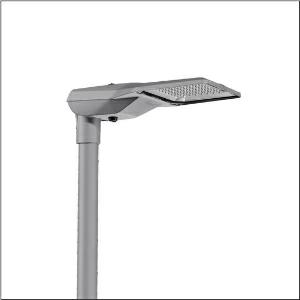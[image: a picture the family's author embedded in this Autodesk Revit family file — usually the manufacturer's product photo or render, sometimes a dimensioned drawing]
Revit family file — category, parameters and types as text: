
# Revit family: streetlight_sl_21_iq_midi___pc-l_5xe3f31y08mb_244c
name_source: partatom
category: Lighting Fixtures
units: mm (PartAtom-declared; Revit-internal decimal feet)

## family parameters
Cut with Voids When Loaded = No
Host = Face
Light Source = No
Part Type = Normal
Room Calculation Point = No
Round Connector Dimension = Use Diameter
Shared = No

## types (1)
- --- (1 x LED, 17070 lm, 129.3 W, 3000K)
    Apparent Load = 129 VA
    CIE Flux Codes = 38 78 98 100 100
    Color Rendering = 70
    Color Temperature = 3000K
    Default Elevation = 1800 mm
    Description = Streetlight SL 21 iQ midi, mast luminaire, primary light control with lens, of PMMA, primary optical cover: cover, of toughened safety glass, transparent, light distribution: PC-L, light emission: direct distribution, primary light characteristic: asymmetric, left, installation type: post-top, side-entry, LED, High Power LED, rated luminous flux: 17.070lm, luminous efficacy: 132lm/W, light colour: 730, colour temperature: 3000K, control: presetting dimming logarithmic, Street-Remote, Auto-Match, Temp-Guard, Lumen-Switch, Night-Set, Smart-Wire, Light-Fading, Desk-Remote (wireless, voltage-free reading and setting of iQ features in the workshop via application-optimized NFC function/RFID function), optimised constant luminous flux control (CLO 2.0), mains connection: 230..240V, AC, 50/60Hz, start of lifetime: 129W, end of service life: 142W, reduction: 56W, luminaire housing, of diecast aluminium, powder-coated, Siteco® metallic grey (DB 702S), corrosivity category C5 mid according to DIN EN ISO 12944, please order mast flange separately, inclination adjustable: 0°, 5°, 10°, 15°, sealing non-destructively replaceable, multi-level sealing system, length: 644mm, width: 335mm, height: 110mm, mast flange for spigot size: 42mm (side-entry): 5XC10008XM4, 60/48mm (side-entry/post-top): 5XC10108XM2, 76/60mm (side-entry/post-top): 5XC10108XM1, Smart Interface below and above, protection rating (complete): IP66, insulation class (complete): insulation class II (safety insulation), certification: CE, ENEC, ENEC+, VDE, impact resistance: IK09, permissible operating ambient temperature for outdoor applications: -40..+50°C, standard-compliant lighting for roads and squares, packaging unit: 1 piece

Light Distribution: PC-L
    Height = 111 mm
    Lamp = 1 x LED
    Lamp Light Flux = 17070 lm
    Lamp Power = 129.3 W
    Lamp count = 1
    Length = 644 mm
    Luminous efficacy = 132 lm/W
    Manufacturer = Siteco
    ModVariant = No
    Model = 5XE3F31Y08MB
    Number of Poles = 1
    OnlyDefault = Yes
    Power Factor = 1
    Product Name = Streetlight SL 21 iQ midi | PC-L
    Product group = mast luminaire | pylon top
    ProductGroupID = 6100
    Protection Class = Protection class II
    Protection Degree = IP 66
    RLX_Detail_Level = 1
    RLX_Emergency_Light_Flux = 0 lm
    RLX_Emergency_Type = 0
    RLX_Emergency_Type_DB = No
    RlxData = <blob elided: 93421 chars, md5=faa4a973>
    Socket = socket
    Standby Power = 0 W
    System Light Flux = 17070 lm
    System Power = 129 W
    Type Comments = factory setting: luminous flux: 100 % | dim-lin: 254 | 672 mA
    Type Image = l_1004304.jpg
    URL = http://relux.com
    VarID = @adj_005637
    Voltage = 0 V
    Weight = 0.00 kg
    Width = 336 mm

## geometry (parser evidence)
native form markers: Blend x4, Sweep x11
no freeform markers — native parametric forms only
